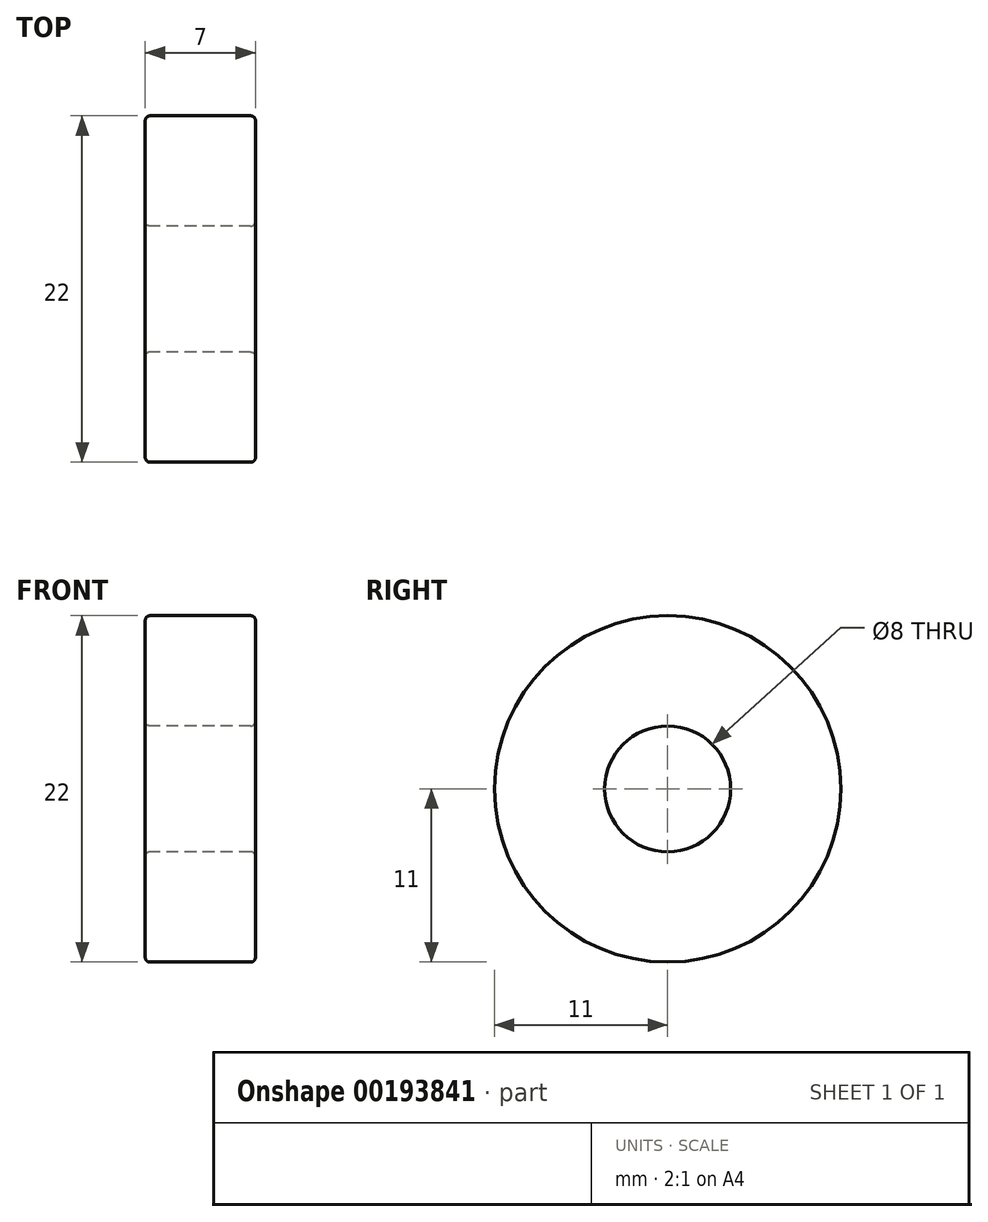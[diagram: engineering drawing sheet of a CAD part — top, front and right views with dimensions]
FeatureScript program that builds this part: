
annotation { "Feature Type Name" : "Feature", "Feature Type Description" : "" }
export const myFeature = defineFeature(function(context is Context, id is Id, definition is map)
    precondition{}
    {
        {
            var Q0;
            Q0=qCreatedBy(makeId("Right.planeOp"),FACE);
            var sketch = newSketch(context, id + "F0", { "sketchPlane" : qUnion([Q0])});
            skCircle(sketch, "E0", {"center": v(0, 0) * mm, "radius": 4 * mm});
            skCircle(sketch, "E1", {"center": v(0, 0) * mm, "radius": 11 * mm});
            skSolve(sketch);
        }
        {
            var Q0;
            Q0=makeQuery(id+"F0.imprint","IMPRINT",FACE,{"disambiguationData":[TD([[makeQuery(id+"F0.imprint","IMPRINT",EDGE,{"derivedFrom":sQuery(id+"F0.wireOp",EDGE,"E0")}),-1.0]])]});
            extrude(context, id + "F1", {"entities" : qUnion([Q0]), "depth" : 7 * mm});
        }
        {
            var Q0;
            Q0=makeQuery(id+"F1.opExtrude","SWEPT_FACE",FACE,{"disambiguationData":[OSD([sQuery(id+"F0.wireOp",EDGE,"E1")])]});
            var Q1;
            Q1=makeQuery(id+"F1.opExtrude","SWEPT_FACE",FACE,{"disambiguationData":[OSD([sQuery(id+"F0.wireOp",EDGE,"E0")])]});
            fillet(context, id + "F2", {"entities" : qUnion([Q0, Q1]), "radius" : 0.3 * mm, "tangentPropagation" : true, "allowEdgeOverflow" : false});
        }
    });
